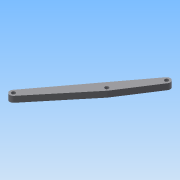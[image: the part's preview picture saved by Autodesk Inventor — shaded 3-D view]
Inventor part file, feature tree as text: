
AUTODESK INVENTOR PART (.ipt)
format: ipt  version: 2015 (Build 190159000, 159)  size: 95,744 bytes
history: native  units: mm
features: extrude x2, sketch x2, other x1
ambient origin geometry x8: Origin, YZ Plane, XZ Plane, XY Plane, X Axis, Y Axis, Z Axis, Center Point
bodies: Body1 (feature_tree)
feature tree (5):
  other  "實體1"
  extrude  "擠出1"  Depth=22.18mm
  extrude  "擠出2"  Depth=14.48mm
  sketch  "草圖1"
  sketch  "草圖2"
